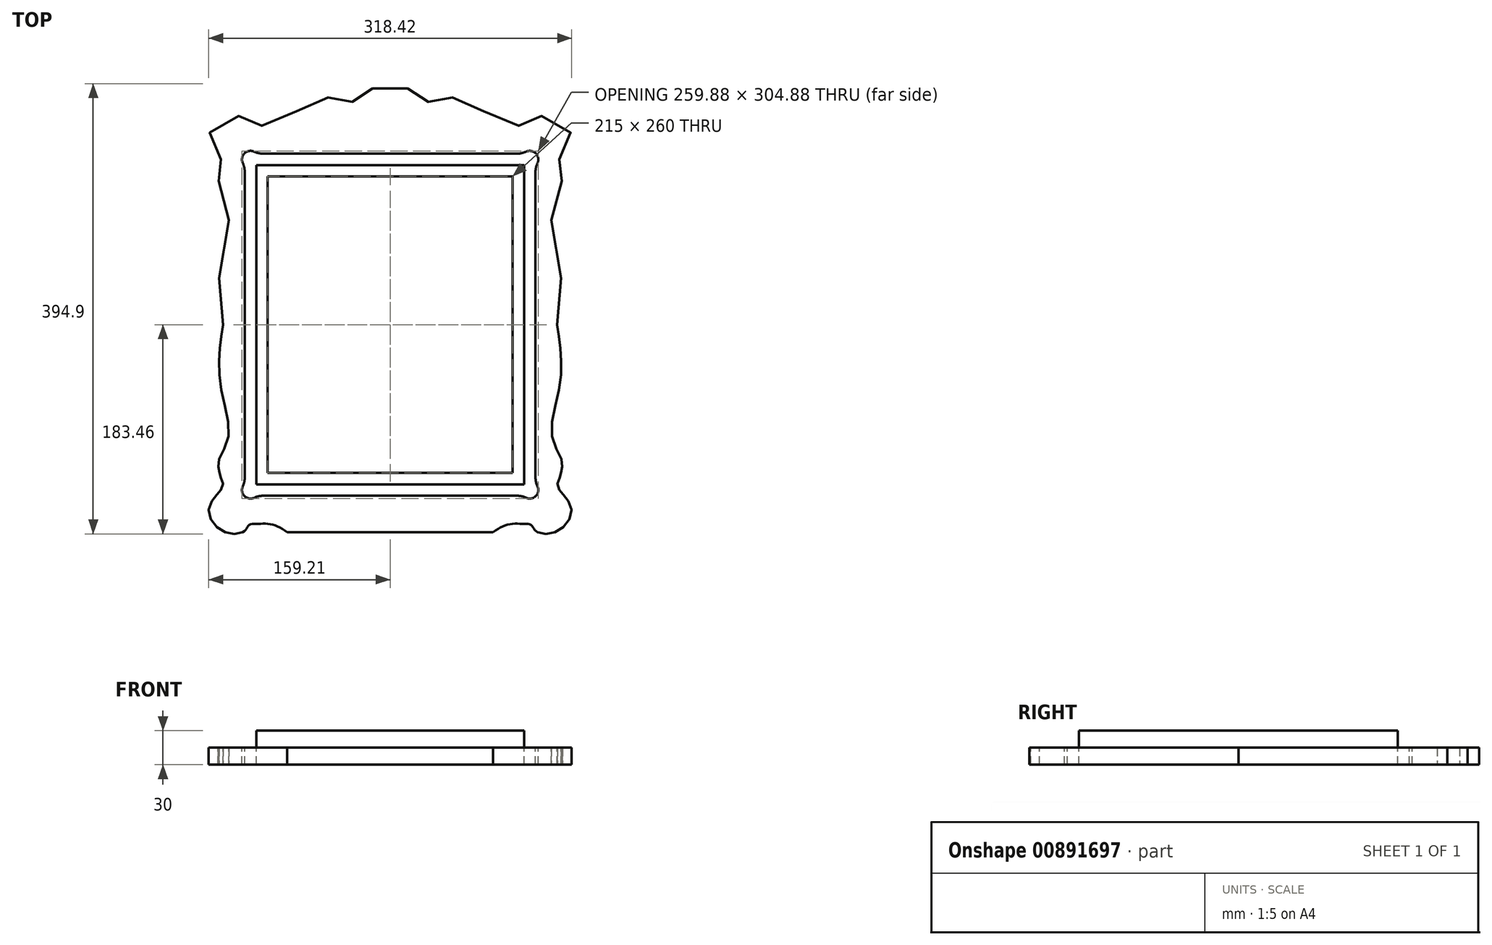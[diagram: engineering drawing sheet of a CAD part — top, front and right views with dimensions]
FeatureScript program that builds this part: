
annotation { "Feature Type Name" : "Feature", "Feature Type Description" : "" }
export const myFeature = defineFeature(function(context is Context, id is Id, definition is map)
    precondition{}
    {
        {
            var Q0;
            Q0=qCreatedBy(makeId("Top.planeOp"),FACE);
            var sketch = newSketch(context, id + "F0", { "sketchPlane" : qUnion([Q0])});
            skPoint(sketch, "E0.0", {"position": v(0, 0) * mm});
            skArc(sketch, "E1.0.0", {"start": v(119.38, 333.82) * mm, "mid": v(127.8, 332.3) * mm, "end": v(129.32, 323.88) * mm});
            skArc(sketch, "E1.0.1", {"start": v(129.32, 323.88) * mm, "mid": v(127.96, 319.8) * mm, "end": v(127.5, 315.54) * mm});
            skLineSegment(sketch, "E1.0.2", {"start": v(127.5, 315.54) * mm, "end": v(127.5, 182) * mm});
            skFitSpline(sketch, "E1.0.5", {"points": [v(146.5, 182) * mm, v(149.6, 206.12) * mm, v(148.09, 239.33) * mm, v(141.97, 280.55) * mm, v(150.87, 302.14) * mm, v(150.08, 309.83) * mm, v(149.2, 315.04) * mm, v(146.76, 320.97) * mm, v(148.7, 327.44) * mm, v(153.43, 332.82) * mm, v(159.2, 345.23) * mm, v(152.22, 359.34) * mm, v(138.51, 365.38) * mm, v(127.66, 362.82) * mm, v(123.75, 357.76) * mm, v(115.5, 356.57) * mm, v(101.19, 357.87) * mm, v(83.98, 368.25) * mm, v(68.12, 375.61) * mm, v(57.61, 380.2) * mm, v(46.5, 382.99) * mm, v(38.39, 380.17) * mm, v(34.33, 377.95) * mm, v(28.58, 376.08) * mm, v(24.82, 380.4) * mm, v(15.24, 389.25) * mm, v(0, 393.44) * mm, v(-15.24, 389.25) * mm, v(-24.82, 380.4) * mm, v(-28.58, 376.08) * mm, v(-34.33, 377.95) * mm, v(-38.39, 380.17) * mm, v(-46.5, 382.99) * mm, v(-57.61, 380.2) * mm, v(-68.12, 375.61) * mm, v(-83.98, 368.25) * mm, v(-101.19, 357.87) * mm, v(-115.5, 356.57) * mm, v(-123.75, 357.76) * mm, v(-127.66, 362.82) * mm, v(-138.51, 365.38) * mm, v(-152.22, 359.34) * mm, v(-159.2, 345.23) * mm, v(-153.43, 332.82) * mm, v(-148.7, 327.44) * mm, v(-146.76, 320.97) * mm, v(-149.2, 315.04) * mm, v(-150.08, 309.83) * mm, v(-150.87, 302.14) * mm, v(-141.97, 280.55) * mm, v(-148.09, 239.33) * mm, v(-149.6, 206.12) * mm, v(-146.5, 182) * mm]});
            skLineSegment(sketch, "E1.0.8", {"start": v(-127.5, 182) * mm, "end": v(-127.5, 315.54) * mm});
            skArc(sketch, "E1.0.9", {"start": v(-127.5, 315.54) * mm, "mid": v(-127.96, 319.8) * mm, "end": v(-129.32, 323.88) * mm});
            skArc(sketch, "E1.0.10", {"start": v(-129.32, 323.88) * mm, "mid": v(-127.8, 332.3) * mm, "end": v(-119.38, 333.82) * mm});
            skArc(sketch, "E1.0.11", {"start": v(-119.38, 333.82) * mm, "mid": v(-115.3, 332.46) * mm, "end": v(-111.04, 332) * mm});
            skLineSegment(sketch, "E1.0.12", {"start": v(-111.04, 332) * mm, "end": v(111.04, 332) * mm});
            skArc(sketch, "E1.0.13", {"start": v(111.04, 332) * mm, "mid": v(115.3, 332.46) * mm, "end": v(119.38, 333.82) * mm});
            skLineSegment(sketch, "E2.0.0", {"start": v(117.5, 322) * mm, "end": v(117.5, 182) * mm});
            skLineSegment(sketch, "E2.0.2", {"start": v(127.5, 182) * mm, "end": v(127.5, 321.4) * mm});
            skArc(sketch, "E2.0.3", {"start": v(127.5, 321.4) * mm, "mid": v(127.8, 332.3) * mm, "end": v(116.9, 332) * mm});
            skLineSegment(sketch, "E2.0.4", {"start": v(116.9, 332) * mm, "end": v(-116.9, 332) * mm});
            skArc(sketch, "E2.0.5", {"start": v(-116.9, 332) * mm, "mid": v(-127.8, 332.3) * mm, "end": v(-127.5, 321.4) * mm});
            skLineSegment(sketch, "E2.0.6", {"start": v(-127.5, 321.4) * mm, "end": v(-127.5, 182) * mm});
            skLineSegment(sketch, "E2.0.8", {"start": v(-117.5, 182) * mm, "end": v(-117.5, 322) * mm});
            skLineSegment(sketch, "E2.0.9", {"start": v(-117.5, 322) * mm, "end": v(117.5, 322) * mm});
            skLineSegment(sketch, "E3.0.0", {"start": v(107.5, 312) * mm, "end": v(107.5, 182) * mm});
            skLineSegment(sketch, "E3.0.2", {"start": v(117.5, 182) * mm, "end": v(117.5, 322) * mm});
            skLineSegment(sketch, "E3.0.3", {"start": v(117.5, 322) * mm, "end": v(-117.5, 322) * mm});
            skLineSegment(sketch, "E3.0.4", {"start": v(-117.5, 322) * mm, "end": v(-117.5, 182) * mm});
            skLineSegment(sketch, "E3.0.6", {"start": v(-107.5, 182) * mm, "end": v(-107.5, 312) * mm});
            skLineSegment(sketch, "E3.0.7", {"start": v(-107.5, 312) * mm, "end": v(107.5, 312) * mm});
            skPoint(sketch, "E1.0.3.end.orphan", {"position": v(146.5, 172) * mm});
            skPoint(sketch, "E4.orphan", {"position": v(117.5, 172) * mm});
            skPoint(sketch, "E5.orphan", {"position": v(127.5, 172) * mm});
            skPoint(sketch, "E6.orphan", {"position": v(107.5, 172) * mm});
            skPoint(sketch, "E7.orphan", {"position": v(-117.5, 172) * mm});
            skPoint(sketch, "E1.0.7.end.orphan", {"position": v(-127.5, 172) * mm});
            skArc(sketch, "E8.MirrorCS", {"start": v(129.32, 40.12) * mm, "mid": v(127.96, 44.2) * mm, "end": v(127.5, 48.46) * mm});
            skArc(sketch, "E9.MirrorCS", {"start": v(111.04, 32) * mm, "mid": v(115.3, 31.54) * mm, "end": v(119.38, 30.18) * mm});
            skArc(sketch, "E10.MirrorCS", {"start": v(127.5, 42.6) * mm, "mid": v(127.8, 31.7) * mm, "end": v(116.9, 32) * mm});
            skArc(sketch, "E11.MirrorCS", {"start": v(-116.9, 32) * mm, "mid": v(-127.8, 31.7) * mm, "end": v(-127.5, 42.6) * mm});
            skArc(sketch, "E12.MirrorCS", {"start": v(119.38, 30.18) * mm, "mid": v(127.8, 31.7) * mm, "end": v(129.32, 40.12) * mm});
            skArc(sketch, "E13.MirrorCS", {"start": v(-119.38, 30.18) * mm, "mid": v(-115.3, 31.54) * mm, "end": v(-111.04, 32) * mm});
            skArc(sketch, "E14.MirrorCS", {"start": v(-129.32, 40.12) * mm, "mid": v(-127.8, 31.7) * mm, "end": v(-119.38, 30.18) * mm});
            skArc(sketch, "E15.MirrorCS", {"start": v(-127.5, 48.46) * mm, "mid": v(-127.96, 44.2) * mm, "end": v(-129.32, 40.12) * mm});
            skLineSegment(sketch, "E16.MirrorCS", {"start": v(127.5, 48.46) * mm, "end": v(127.5, 182) * mm});
            skLineSegment(sketch, "E17.MirrorCS", {"start": v(-111.04, 32) * mm, "end": v(111.04, 32) * mm});
            skPoint(sketch, "E18.MirrorP", {"position": v(117.5, 192) * mm});
            skLineSegment(sketch, "E19.MirrorCS", {"start": v(-127.5, 182) * mm, "end": v(-127.5, 48.46) * mm});
            skLineSegment(sketch, "E20.MirrorCS", {"start": v(-117.5, 42) * mm, "end": v(-117.5, 182) * mm});
            skLineSegment(sketch, "E21.MirrorCS", {"start": v(117.5, 42) * mm, "end": v(-117.5, 42) * mm});
            skPoint(sketch, "E22.MirrorP", {"position": v(127.5, 192) * mm});
            skLineSegment(sketch, "E23.MirrorCS", {"start": v(117.5, 182) * mm, "end": v(117.5, 42) * mm});
            skPoint(sketch, "E24.MirrorP", {"position": v(107.5, 192) * mm});
            skPoint(sketch, "E25.MirrorP", {"position": v(146.5, 192) * mm});
            skLineSegment(sketch, "E26.MirrorCS", {"start": v(-107.5, 52) * mm, "end": v(107.5, 52) * mm});
            skPoint(sketch, "E27.MirrorP", {"position": v(-117.5, 192) * mm});
            skLineSegment(sketch, "E28.MirrorCS", {"start": v(127.5, 182) * mm, "end": v(127.5, 42.6) * mm});
            skPoint(sketch, "E29.MirrorP", {"position": v(-127.5, 192) * mm});
            skLineSegment(sketch, "E30.MirrorCS", {"start": v(-117.5, 182) * mm, "end": v(-117.5, 42) * mm});
            skLineSegment(sketch, "E31.MirrorCS", {"start": v(107.5, 52) * mm, "end": v(107.5, 182) * mm});
            skLineSegment(sketch, "E32.MirrorCS", {"start": v(-127.5, 42.6) * mm, "end": v(-127.5, 182) * mm});
            skLineSegment(sketch, "E33.MirrorCS", {"start": v(-107.5, 182) * mm, "end": v(-107.5, 52) * mm});
            skFitSpline(sketch, "E34.MirrorCS", {"points": [v(146.5, 182) * mm, v(149.6, 157.88) * mm, v(148.09, 124.67) * mm, v(141.97, 83.45) * mm, v(150.87, 61.86) * mm, v(150.08, 54.17) * mm, v(149.2, 48.96) * mm, v(146.76, 43.03) * mm, v(148.7, 36.56) * mm, v(153.43, 31.18) * mm, v(159.2, 18.77) * mm, v(152.22, 4.66) * mm, v(138.51, -1.38) * mm, v(127.66, 1.18) * mm, v(123.75, 6.24) * mm, v(115.5, 7.43) * mm, v(101.19, 6.13) * mm, v(83.98, -4.25) * mm, v(68.12, -11.61) * mm, v(57.61, -16.2) * mm, v(46.5, -18.99) * mm, v(38.39, -16.17) * mm, v(34.33, -13.95) * mm, v(28.58, -12.08) * mm, v(24.82, -16.4) * mm, v(15.24, -25.25) * mm, v(0, -29.44) * mm, v(-15.24, -25.25) * mm, v(-24.82, -16.4) * mm, v(-28.58, -12.08) * mm, v(-34.33, -13.95) * mm, v(-38.39, -16.17) * mm, v(-46.5, -18.99) * mm, v(-57.61, -16.2) * mm, v(-68.12, -11.61) * mm, v(-83.98, -4.25) * mm, v(-101.19, 6.13) * mm, v(-115.5, 7.43) * mm, v(-123.75, 6.24) * mm, v(-127.66, 1.18) * mm, v(-138.51, -1.38) * mm, v(-152.22, 4.66) * mm, v(-159.2, 18.77) * mm, v(-153.43, 31.18) * mm, v(-148.7, 36.56) * mm, v(-146.76, 43.03) * mm, v(-149.2, 48.96) * mm, v(-150.08, 54.17) * mm, v(-150.87, 61.86) * mm, v(-141.97, 83.45) * mm, v(-148.09, 124.67) * mm, v(-149.6, 157.88) * mm, v(-146.5, 182) * mm]});
            skLineSegment(sketch, "E35.MirrorCS", {"start": v(116.9, 32) * mm, "end": v(-116.9, 32) * mm});
            skLineSegment(sketch, "E36.MirrorCS", {"start": v(117.5, 42) * mm, "end": v(117.5, 182) * mm});
            skLineSegment(sketch, "E37.MirrorCS", {"start": v(-117.5, 42) * mm, "end": v(117.5, 42) * mm});
            skLineSegment(sketch, "E38.0", {"start": v(-138, 0) * mm, "end": v(138, 0) * mm});
            skFitSpline(sketch, "E39.trimOffspring", {"points": [v(146.5, 182) * mm, v(149.6, 157.88) * mm, v(148.09, 124.67) * mm, v(141.97, 83.45) * mm, v(150.87, 61.86) * mm, v(150.08, 54.17) * mm, v(149.2, 48.96) * mm, v(146.76, 43.03) * mm, v(148.7, 36.56) * mm, v(153.43, 31.18) * mm, v(159.2, 18.77) * mm, v(152.22, 4.66) * mm, v(138.51, -1.38) * mm, v(127.66, 1.18) * mm, v(123.75, 6.24) * mm, v(115.5, 7.43) * mm, v(101.19, 6.13) * mm, v(83.98, -4.25) * mm, v(68.12, -11.61) * mm, v(57.61, -16.2) * mm, v(46.5, -18.99) * mm, v(38.39, -16.17) * mm, v(34.33, -13.95) * mm, v(28.58, -12.08) * mm, v(24.82, -16.4) * mm, v(15.24, -25.25) * mm, v(0, -29.44) * mm, v(-15.24, -25.25) * mm, v(-24.82, -16.4) * mm, v(-28.58, -12.08) * mm, v(-34.33, -13.95) * mm, v(-38.39, -16.17) * mm, v(-46.5, -18.99) * mm, v(-57.61, -16.2) * mm, v(-68.12, -11.61) * mm, v(-83.98, -4.25) * mm, v(-101.19, 6.13) * mm, v(-115.5, 7.43) * mm, v(-123.75, 6.24) * mm, v(-127.66, 1.18) * mm, v(-138.51, -1.38) * mm, v(-152.22, 4.66) * mm, v(-159.2, 18.77) * mm, v(-153.43, 31.18) * mm, v(-148.7, 36.56) * mm, v(-146.76, 43.03) * mm, v(-149.2, 48.96) * mm, v(-150.08, 54.17) * mm, v(-150.87, 61.86) * mm, v(-141.97, 83.45) * mm, v(-148.09, 124.67) * mm, v(-149.6, 157.88) * mm, v(-146.5, 182) * mm]});
            skSolve(sketch);
        }
        {
            var Q0;
            {var subQ19=sQuery(id+"F0.wireOp",EDGE,"E1.0.1");Q0=makeQuery(id+"F0.imprint","IMPRINT",FACE,{"disambiguationData":[TD([[makeQuery(id+"F0.imprint","IMPRINT",EDGE,{"derivedFrom":subQ19}),1.0]])]});}
            var Q1;
            Q1=makeQuery(id+"F0.imprint","IMPRINT",FACE,{"disambiguationData":[TD([[makeQuery(id+"F0.imprint","IMPRINT",EDGE,{"derivedFrom":sQuery(id+"F0.wireOp",EDGE,"E3.0.2")}),-1.0]])]});
            var Q2;
            Q2=makeQuery(id+"F0.imprint","IMPRINT",FACE,{"disambiguationData":[TD([[makeQuery(id+"F0.imprint","IMPRINT",EDGE,{"derivedFrom":sQuery(id+"F0.wireOp",EDGE,"E3.0.0")}),1.0]])]});
            extrude(context, id + "F1", {"entities" : qUnion([Q0, Q1, Q2]), "oppositeDirection" : true, "depth" : 15 * mm, "offsetDistance" : 25 * mm});
        }
        {
            var Q0;
            Q0=makeQuery(id+"F0.imprint","IMPRINT",FACE,{"disambiguationData":[TD([[makeQuery(id+"F0.imprint","IMPRINT",EDGE,{"derivedFrom":sQuery(id+"F0.wireOp",EDGE,"E3.0.2")}),-1.0]])]});
            var Q1;
            Q1=makeQuery(id+"F0.imprint","IMPRINT",FACE,{"disambiguationData":[TD([[makeQuery(id+"F0.imprint","IMPRINT",EDGE,{"derivedFrom":sQuery(id+"F0.wireOp",EDGE,"E3.0.0")}),1.0]])]});
            extrude(context, id + "F2", {"entities" : qUnion([Q0, Q1]), "operationType" : NewBodyOperationType.ADD, "depth" : 10 * mm, "offsetDistance" : 25 * mm});
        }
        {
            var Q0;
            Q0=makeQuery(id+"F2.opExtrude","CAP_FACE",FACE,{"disambiguationData":[OSD([sQuery(id+"F0.wireOp",EDGE,"E2.0.2"),sQuery(id+"F0.wireOp",EDGE,"E2.0.3"),sQuery(id+"F0.wireOp",EDGE,"E2.0.4"),sQuery(id+"F0.wireOp",EDGE,"E2.0.5"),sQuery(id+"F0.wireOp",EDGE,"E2.0.6"),sQuery(id+"F0.wireOp",EDGE,"E3.0.0"),sQuery(id+"F0.wireOp",EDGE,"E3.0.6"),sQuery(id+"F0.wireOp",EDGE,"E3.0.7"),sQuery(id+"F0.wireOp",EDGE,"E10.MirrorCS"),sQuery(id+"F0.wireOp",EDGE,"E11.MirrorCS"),sQuery(id+"F0.wireOp",EDGE,"E12.MirrorCS"),sQuery(id+"F0.wireOp",EDGE,"E14.MirrorCS"),sQuery(id+"F0.wireOp",EDGE,"E26.MirrorCS"),sQuery(id+"F0.wireOp",EDGE,"E28.MirrorCS"),sQuery(id+"F0.wireOp",EDGE,"E31.MirrorCS"),sQuery(id+"F0.wireOp",EDGE,"E32.MirrorCS"),sQuery(id+"F0.wireOp",EDGE,"E33.MirrorCS"),sQuery(id+"F0.wireOp",EDGE,"E35.MirrorCS")])],"isStart":false});
            var sketch = newSketch(context, id + "F3", { "sketchPlane" : qUnion([Q0])});
            skLineSegment(sketch, "E40.0", {"start": v(-117.5, 322) * mm, "end": v(117.5, 322) * mm});
            skLineSegment(sketch, "E41.0", {"start": v(117.5, 322) * mm, "end": v(117.5, 182) * mm});
            skLineSegment(sketch, "E42.0", {"start": v(117.5, 182) * mm, "end": v(117.5, 42) * mm});
            skLineSegment(sketch, "E43.0", {"start": v(-117.5, 42) * mm, "end": v(117.5, 42) * mm});
            skLineSegment(sketch, "E44.0", {"start": v(-117.5, 42) * mm, "end": v(-117.5, 182) * mm});
            skLineSegment(sketch, "E45.0", {"start": v(-117.5, 182) * mm, "end": v(-117.5, 322) * mm});
            skSolve(sketch);
        }
        {
            var Q0;
            Q0=makeQuery(id+"F3.imprint","IMPRINT",FACE,{"disambiguationData":[TD([[makeQuery(id+"F3.imprint","IMPRINT",EDGE,{"derivedFrom":sQuery(id+"F3.wireOp",EDGE,"E40.0")}),-1.0]])]});
            extrude(context, id + "F4", {"entities" : qUnion([Q0]), "operationType" : NewBodyOperationType.ADD, "depth" : 5 * mm, "offsetDistance" : 25 * mm});
        }
    });
